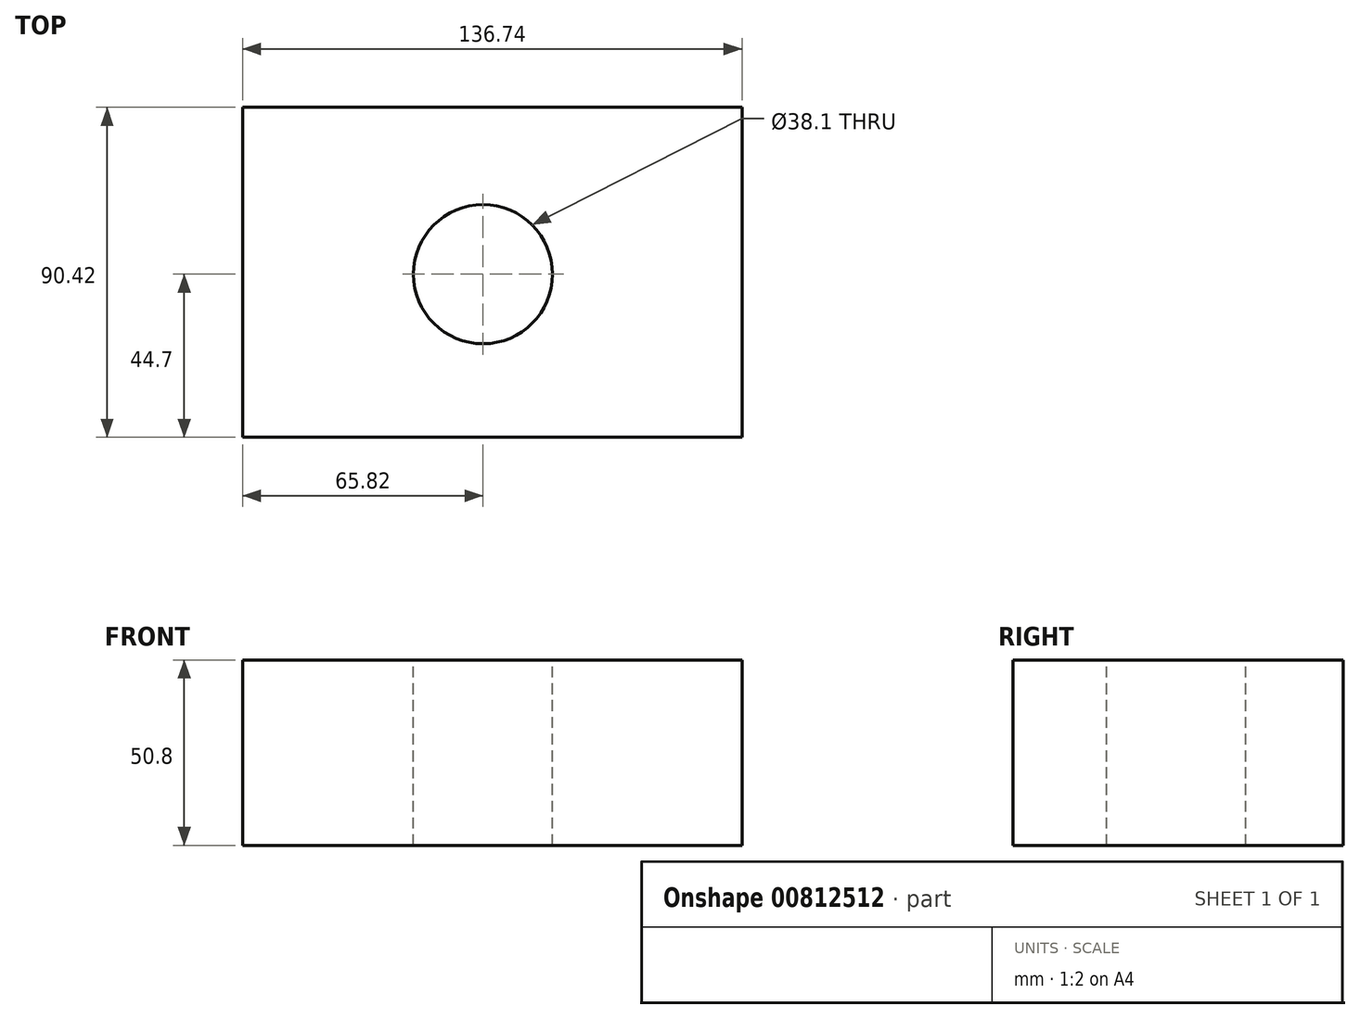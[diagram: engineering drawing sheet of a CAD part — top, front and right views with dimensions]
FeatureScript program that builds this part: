
annotation { "Feature Type Name" : "Feature", "Feature Type Description" : "" }
export const myFeature = defineFeature(function(context is Context, id is Id, definition is map)
    precondition{}
    {
        {
            var Q0;
            Q0=qCreatedBy(makeId("Top.planeOp"),FACE);
            var sketch = newSketch(context, id + "F0", { "sketchPlane" : qUnion([Q0])});
            skLineSegment(sketch, "E0.bottom", {"start": v(-65.82, -44.7) * mm, "end": v(70.92, -44.7) * mm});
            skLineSegment(sketch, "E0.top", {"start": v(-65.82, 45.72) * mm, "end": v(70.92, 45.72) * mm});
            skLineSegment(sketch, "E0.left", {"start": v(-65.82, -44.7) * mm, "end": v(-65.82, 45.72) * mm});
            skLineSegment(sketch, "E0.right", {"start": v(70.92, -44.7) * mm, "end": v(70.92, 45.72) * mm});
            skCircle(sketch, "E1", {"center": v(0, 0) * mm, "radius": 19.05 * mm});
            skSolve(sketch);
        }
        {
            var Q0;
            Q0=makeQuery(id+"F0.imprint","IMPRINT",FACE,{"disambiguationData":[TD([[makeQuery(id+"F0.imprint","IMPRINT",EDGE,{"derivedFrom":sQuery(id+"F0.wireOp",EDGE,"E0.bottom")}),1.0]])]});
            extrude(context, id + "F1", {"entities" : qUnion([Q0]), "oppositeDirection" : true, "depth" : 50.8 * mm, "offsetDistance" : 25.4 * mm});
        }
    });
